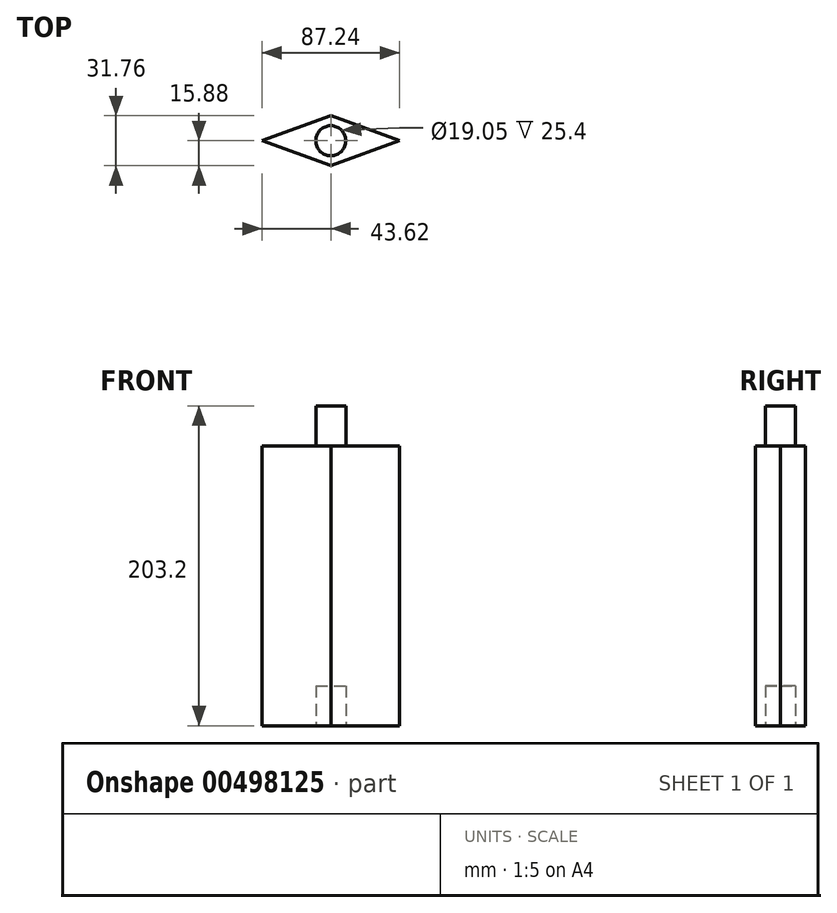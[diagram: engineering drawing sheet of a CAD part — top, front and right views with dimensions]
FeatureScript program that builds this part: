
annotation { "Feature Type Name" : "Feature", "Feature Type Description" : "" }
export const myFeature = defineFeature(function(context is Context, id is Id, definition is map)
    precondition{}
    {
        {
            var Q0;
            Q0=qCreatedBy(makeId("Top.planeOp"),FACE);
            var sketch = newSketch(context, id + "F0", { "sketchPlane" : qUnion([Q0])});
            skLineSegment(sketch, "E0.bottom", {"start": v(50.8, 15.88) * mm, "end": v(-50.8, 15.88) * mm});
            skLineSegment(sketch, "E0.top", {"start": v(50.8, -15.88) * mm, "end": v(-50.8, -15.88) * mm});
            skLineSegment(sketch, "E0.left", {"start": v(50.8, 15.88) * mm, "end": v(50.8, -15.88) * mm});
            skLineSegment(sketch, "E0.right", {"start": v(-50.8, 15.88) * mm, "end": v(-50.8, -15.88) * mm});
            skPoint(sketch, "E0.middle", {"position": v(0, 0) * mm});
            skSolve(sketch);
        }
        {
            var Q0;
            Q0=makeQuery(id+"F0.imprint","IMPRINT",FACE,{"disambiguationData":[TD([[makeQuery(id+"F0.imprint","IMPRINT",EDGE,{"derivedFrom":sQuery(id+"F0.wireOp",EDGE,"E0.bottom")}),1.0]])]});
            extrude(context, id + "F1", {"entities" : qUnion([Q0]), "depth" : 177.8 * mm, "offsetDistance" : 25.4 * mm});
        }
        {
            var Q0;
            Q0=makeQuery(id+"F1.opExtrude","SWEPT_EDGE",EDGE,{"disambiguationData":[OSD([sQuery(id+"F0.wireOp",EDGE,"E0.bottom"),sQuery(id+"F0.wireOp",EDGE,"E0.left")])]});
            var Q1;
            Q1=makeQuery(id+"F1.opExtrude","SWEPT_EDGE",EDGE,{"disambiguationData":[OSD([sQuery(id+"F0.wireOp",EDGE,"E0.top"),sQuery(id+"F0.wireOp",EDGE,"E0.left")])]});
            var Q2;
            Q2=makeQuery(id+"F1.opExtrude","SWEPT_EDGE",EDGE,{"disambiguationData":[OSD([sQuery(id+"F0.wireOp",EDGE,"E0.top"),sQuery(id+"F0.wireOp",EDGE,"E0.right")])]});
            var Q3;
            Q3=makeQuery(id+"F1.opExtrude","SWEPT_EDGE",EDGE,{"disambiguationData":[OSD([sQuery(id+"F0.wireOp",EDGE,"E0.bottom"),sQuery(id+"F0.wireOp",EDGE,"E0.right")])]});
            chamfer(context, id + "F2", {"entities" : qUnion([Q0, Q1, Q2, Q3]), "chamferType" : ChamferType.OFFSET_ANGLE, "width" : 50.8 * mm, "oppositeDirection" : false, "angle" : 20 * degree, "tangentPropagation" : true});
        }
        {
            var Q0;
            Q0=makeQuery(id+"F1.opExtrude","CAP_FACE",FACE,{"disambiguationData":[OSD([sQuery(id+"F0.wireOp",EDGE,"E0.bottom"),sQuery(id+"F0.wireOp",EDGE,"E0.top"),sQuery(id+"F0.wireOp",EDGE,"E0.left"),sQuery(id+"F0.wireOp",EDGE,"E0.right")])],"isStart":false});
            var sketch = newSketch(context, id + "F3", { "sketchPlane" : qUnion([Q0])});
            skCircle(sketch, "E1", {"center": v(0, 0) * mm, "radius": 9.53 * mm});
            skSolve(sketch);
        }
        {
            var Q0;
            Q0 = qSketchRegion(id + "F3", true);
            extrude(context, id + "F4", {"entities" : qUnion([Q0]), "operationType" : NewBodyOperationType.ADD, "depth" : 25.4 * mm, "offsetDistance" : 25.4 * mm});
        }
        {
            var Q0;
            Q0=makeQuery(id+"F1.opExtrude","CAP_FACE",FACE,{"disambiguationData":[OSD([sQuery(id+"F0.wireOp",EDGE,"E0.bottom"),sQuery(id+"F0.wireOp",EDGE,"E0.top"),sQuery(id+"F0.wireOp",EDGE,"E0.left"),sQuery(id+"F0.wireOp",EDGE,"E0.right")])],"isStart":true});
            var sketch = newSketch(context, id + "F5", { "sketchPlane" : qUnion([Q0])});
            skCircle(sketch, "E2", {"center": v(0, 0) * mm, "radius": 9.53 * mm});
            skSolve(sketch);
        }
        {
            var Q0;
            Q0 = qSketchRegion(id + "F5", true);
            extrude(context, id + "F6", {"entities" : qUnion([Q0]), "operationType" : NewBodyOperationType.REMOVE, "oppositeDirection" : true, "depth" : 25.4 * mm, "offsetDistance" : 25.4 * mm});
        }
    });
